# Revit family: 306_668fb259bbc246529dc69d010db632
name_source: partatom
category: Pipe Accessories
units: mm (PartAtom-declared; Revit-internal decimal feet)

## family parameters
Always vertical = Yes
Cut with Voids When Loaded = No
Part Type = Valve - Breaks Into
Round Connector Dimension = Use Diameter
Shared = No
Work Plane-Based = No

## types (57) — shared parameters
Description = 6-way characterised control valve, Internal thread
L2D_Min = 3048 mm  [stored 10 ft]
Manufacturer = Belimo
QmdConnectorList = 301;D;302;D;303;D;304;D;305;D;306;D
R3 = 10 mm  [stored 0.0328084 ft]
R5 = 15 mm  [stored 0.0492126 ft]
S1 = 43 mm  [stored 0.141076 ft]
S2 = 22 mm  [stored 0.0721785 ft]
S3 = 42 mm  [stored 0.137795 ft]
magiPartTypeId = 306
magiProductFamilyId = 668fb259bbc246529dc69d010db632

## per-type parameters (varying)
| type | CenSd_R_6 | D | H | H1 | H2 | H3 | H3__ve | L1 | L1__ve | L2 | L2D | L2__ve | LL | LY1 | LY1__ve | R | R1 | R2 | W2D | magiProductId |
| R3015-1-1-B2 | 10 mm  [stored 0.0328084 ft] | 15 mm | 119 mm  [stored 0.39042 ft] | 45 mm  [stored 0.147638 ft] | 47 mm  [stored 0.154199 ft] | 114 mm  [stored 0.374016 ft] | -114 mm  [stored -0.374016 ft] | 16 mm | -16 mm | 32 mm  [stored 0.104987 ft] | 79 mm | -32 mm | 40 mm  [stored 0.131234 ft] | 15 mm  [stored 0.0492126 ft] | -15 mm  [stored -0.0492126 ft] | 11 mm  [stored 0.0360892 ft] | 9 mm  [stored 0.0295276 ft] | 18 mm | 15 mm  [stored 0.0492126 ft] | 03fa744958c748f3845fa2f35dbf64 |
| R3020-P63-4-B2 | 13 mm | 20 mm | 148 mm  [stored 0.485564 ft] | 59 mm  [stored 0.19357 ft] | 54 mm  [stored 0.177165 ft] | 143 mm  [stored 0.46916 ft] | -143 mm  [stored -0.46916 ft] | 20 mm  [stored 0.0656168 ft] | -20 mm  [stored -0.0656168 ft] | 40 mm  [stored 0.131234 ft] | 100 mm  [stored 0.328084 ft] | -40 mm  [stored -0.131234 ft] | 50 mm  [stored 0.164042 ft] | 18 mm | -18 mm | 15 mm  [stored 0.0492126 ft] | 13 mm | 25 mm  [stored 0.082021 ft] | 20 mm  [stored 0.0656168 ft] | 66261c9dc02143649f8cac8046c0c7 |
| R3020-P63-2P5-B2 | 13 mm | 20 mm | 148 mm  [stored 0.485564 ft] | 59 mm  [stored 0.19357 ft] | 54 mm  [stored 0.177165 ft] | 143 mm  [stored 0.46916 ft] | -143 mm  [stored -0.46916 ft] | 20 mm  [stored 0.0656168 ft] | -20 mm  [stored -0.0656168 ft] | 40 mm  [stored 0.131234 ft] | 100 mm  [stored 0.328084 ft] | -40 mm  [stored -0.131234 ft] | 50 mm  [stored 0.164042 ft] | 18 mm | -18 mm | 15 mm  [stored 0.0492126 ft] | 13 mm | 25 mm  [stored 0.082021 ft] | 20 mm  [stored 0.0656168 ft] | 6e03b1389a624df6b33623b2063c5b |
| R3020-P63-1P6-B2 | 13 mm | 20 mm | 148 mm  [stored 0.485564 ft] | 59 mm  [stored 0.19357 ft] | 54 mm  [stored 0.177165 ft] | 143 mm  [stored 0.46916 ft] | -143 mm  [stored -0.46916 ft] | 20 mm  [stored 0.0656168 ft] | -20 mm  [stored -0.0656168 ft] | 40 mm  [stored 0.131234 ft] | 100 mm  [stored 0.328084 ft] | -40 mm  [stored -0.131234 ft] | 50 mm  [stored 0.164042 ft] | 18 mm | -18 mm | 15 mm  [stored 0.0492126 ft] | 13 mm | 25 mm  [stored 0.082021 ft] | 20 mm  [stored 0.0656168 ft] | fbef73f2dd7a4f4cae0204b01a27d9 |
| R3020-4-P63-B2 | 13 mm | 20 mm | 148 mm  [stored 0.485564 ft] | 59 mm  [stored 0.19357 ft] | 54 mm  [stored 0.177165 ft] | 143 mm  [stored 0.46916 ft] | -143 mm  [stored -0.46916 ft] | 20 mm  [stored 0.0656168 ft] | -20 mm  [stored -0.0656168 ft] | 40 mm  [stored 0.131234 ft] | 100 mm  [stored 0.328084 ft] | -40 mm  [stored -0.131234 ft] | 50 mm  [stored 0.164042 ft] | 18 mm | -18 mm | 15 mm  [stored 0.0492126 ft] | 13 mm | 25 mm  [stored 0.082021 ft] | 20 mm  [stored 0.0656168 ft] | ab1cd6763b854cb2a57e6034a10ecb |
| R3020-4-4-B2 | 13 mm | 20 mm | 148 mm  [stored 0.485564 ft] | 59 mm  [stored 0.19357 ft] | 54 mm  [stored 0.177165 ft] | 143 mm  [stored 0.46916 ft] | -143 mm  [stored -0.46916 ft] | 20 mm  [stored 0.0656168 ft] | -20 mm  [stored -0.0656168 ft] | 40 mm  [stored 0.131234 ft] | 100 mm  [stored 0.328084 ft] | -40 mm  [stored -0.131234 ft] | 50 mm  [stored 0.164042 ft] | 18 mm | -18 mm | 15 mm  [stored 0.0492126 ft] | 13 mm | 25 mm  [stored 0.082021 ft] | 20 mm  [stored 0.0656168 ft] | 5eca1c81c0fd4f1fafaa62e16ba6c2 |
| R3020-4-2P5-B2 | 13 mm | 20 mm | 148 mm  [stored 0.485564 ft] | 59 mm  [stored 0.19357 ft] | 54 mm  [stored 0.177165 ft] | 143 mm  [stored 0.46916 ft] | -143 mm  [stored -0.46916 ft] | 20 mm  [stored 0.0656168 ft] | -20 mm  [stored -0.0656168 ft] | 40 mm  [stored 0.131234 ft] | 100 mm  [stored 0.328084 ft] | -40 mm  [stored -0.131234 ft] | 50 mm  [stored 0.164042 ft] | 18 mm | -18 mm | 15 mm  [stored 0.0492126 ft] | 13 mm | 25 mm  [stored 0.082021 ft] | 20 mm  [stored 0.0656168 ft] | 8c2a2468e35046a99a0da62e88bc71 |
| R3020-4-1P6-B2 | 13 mm | 20 mm | 148 mm  [stored 0.485564 ft] | 59 mm  [stored 0.19357 ft] | 54 mm  [stored 0.177165 ft] | 143 mm  [stored 0.46916 ft] | -143 mm  [stored -0.46916 ft] | 20 mm  [stored 0.0656168 ft] | -20 mm  [stored -0.0656168 ft] | 40 mm  [stored 0.131234 ft] | 100 mm  [stored 0.328084 ft] | -40 mm  [stored -0.131234 ft] | 50 mm  [stored 0.164042 ft] | 18 mm | -18 mm | 15 mm  [stored 0.0492126 ft] | 13 mm | 25 mm  [stored 0.082021 ft] | 20 mm  [stored 0.0656168 ft] | 6e0713c00b33463ea5d84b7bfd9a89 |
| R3020-4-1-B2 | 13 mm | 20 mm | 148 mm  [stored 0.485564 ft] | 59 mm  [stored 0.19357 ft] | 54 mm  [stored 0.177165 ft] | 143 mm  [stored 0.46916 ft] | -143 mm  [stored -0.46916 ft] | 20 mm  [stored 0.0656168 ft] | -20 mm  [stored -0.0656168 ft] | 40 mm  [stored 0.131234 ft] | 100 mm  [stored 0.328084 ft] | -40 mm  [stored -0.131234 ft] | 50 mm  [stored 0.164042 ft] | 18 mm | -18 mm | 15 mm  [stored 0.0492126 ft] | 13 mm | 25 mm  [stored 0.082021 ft] | 20 mm  [stored 0.0656168 ft] | cf51fe3bf48d42a19b5262bd151528 |
| R3020-2P5-P63-B2 | 13 mm | 20 mm | 148 mm  [stored 0.485564 ft] | 59 mm  [stored 0.19357 ft] | 54 mm  [stored 0.177165 ft] | 143 mm  [stored 0.46916 ft] | -143 mm  [stored -0.46916 ft] | 20 mm  [stored 0.0656168 ft] | -20 mm  [stored -0.0656168 ft] | 40 mm  [stored 0.131234 ft] | 100 mm  [stored 0.328084 ft] | -40 mm  [stored -0.131234 ft] | 50 mm  [stored 0.164042 ft] | 18 mm | -18 mm | 15 mm  [stored 0.0492126 ft] | 13 mm | 25 mm  [stored 0.082021 ft] | 20 mm  [stored 0.0656168 ft] | 087235409c174f2a97f6a175d805da |
| R3020-2P5-4-B2 | 13 mm | 20 mm | 148 mm  [stored 0.485564 ft] | 59 mm  [stored 0.19357 ft] | 54 mm  [stored 0.177165 ft] | 143 mm  [stored 0.46916 ft] | -143 mm  [stored -0.46916 ft] | 20 mm  [stored 0.0656168 ft] | -20 mm  [stored -0.0656168 ft] | 40 mm  [stored 0.131234 ft] | 100 mm  [stored 0.328084 ft] | -40 mm  [stored -0.131234 ft] | 50 mm  [stored 0.164042 ft] | 18 mm | -18 mm | 15 mm  [stored 0.0492126 ft] | 13 mm | 25 mm  [stored 0.082021 ft] | 20 mm  [stored 0.0656168 ft] | 58d16455c4a143a0a09fdc7f0ee0a8 |
| R3020-2P5-2P5-B2 | 13 mm | 20 mm | 148 mm  [stored 0.485564 ft] | 59 mm  [stored 0.19357 ft] | 54 mm  [stored 0.177165 ft] | 143 mm  [stored 0.46916 ft] | -143 mm  [stored -0.46916 ft] | 20 mm  [stored 0.0656168 ft] | -20 mm  [stored -0.0656168 ft] | 40 mm  [stored 0.131234 ft] | 100 mm  [stored 0.328084 ft] | -40 mm  [stored -0.131234 ft] | 50 mm  [stored 0.164042 ft] | 18 mm | -18 mm | 15 mm  [stored 0.0492126 ft] | 13 mm | 25 mm  [stored 0.082021 ft] | 20 mm  [stored 0.0656168 ft] | 091caa0dfde748a884ceec14c542ad |
| R3020-2P5-1P6-B2 | 13 mm | 20 mm | 148 mm  [stored 0.485564 ft] | 59 mm  [stored 0.19357 ft] | 54 mm  [stored 0.177165 ft] | 143 mm  [stored 0.46916 ft] | -143 mm  [stored -0.46916 ft] | 20 mm  [stored 0.0656168 ft] | -20 mm  [stored -0.0656168 ft] | 40 mm  [stored 0.131234 ft] | 100 mm  [stored 0.328084 ft] | -40 mm  [stored -0.131234 ft] | 50 mm  [stored 0.164042 ft] | 18 mm | -18 mm | 15 mm  [stored 0.0492126 ft] | 13 mm | 25 mm  [stored 0.082021 ft] | 20 mm  [stored 0.0656168 ft] | 1ec0d4dad9a34521b66bef19604ba6 |
| R3020-2P5-1-B2 | 13 mm | 20 mm | 148 mm  [stored 0.485564 ft] | 59 mm  [stored 0.19357 ft] | 54 mm  [stored 0.177165 ft] | 143 mm  [stored 0.46916 ft] | -143 mm  [stored -0.46916 ft] | 20 mm  [stored 0.0656168 ft] | -20 mm  [stored -0.0656168 ft] | 40 mm  [stored 0.131234 ft] | 100 mm  [stored 0.328084 ft] | -40 mm  [stored -0.131234 ft] | 50 mm  [stored 0.164042 ft] | 18 mm | -18 mm | 15 mm  [stored 0.0492126 ft] | 13 mm | 25 mm  [stored 0.082021 ft] | 20 mm  [stored 0.0656168 ft] | cbbfb14f2a6e4f6f92310ec71a4552 |
| R3020-1P6-P63-B2 | 13 mm | 20 mm | 148 mm  [stored 0.485564 ft] | 59 mm  [stored 0.19357 ft] | 54 mm  [stored 0.177165 ft] | 143 mm  [stored 0.46916 ft] | -143 mm  [stored -0.46916 ft] | 20 mm  [stored 0.0656168 ft] | -20 mm  [stored -0.0656168 ft] | 40 mm  [stored 0.131234 ft] | 100 mm  [stored 0.328084 ft] | -40 mm  [stored -0.131234 ft] | 50 mm  [stored 0.164042 ft] | 18 mm | -18 mm | 15 mm  [stored 0.0492126 ft] | 13 mm | 25 mm  [stored 0.082021 ft] | 20 mm  [stored 0.0656168 ft] | 7b8e98678cfe4800af13abc20189e0 |
| R3020-1P6-4-B2 | 13 mm | 20 mm | 148 mm  [stored 0.485564 ft] | 59 mm  [stored 0.19357 ft] | 54 mm  [stored 0.177165 ft] | 143 mm  [stored 0.46916 ft] | -143 mm  [stored -0.46916 ft] | 20 mm  [stored 0.0656168 ft] | -20 mm  [stored -0.0656168 ft] | 40 mm  [stored 0.131234 ft] | 100 mm  [stored 0.328084 ft] | -40 mm  [stored -0.131234 ft] | 50 mm  [stored 0.164042 ft] | 18 mm | -18 mm | 15 mm  [stored 0.0492126 ft] | 13 mm | 25 mm  [stored 0.082021 ft] | 20 mm  [stored 0.0656168 ft] | 45ff41b9d2724979a5d0f47ae0925d |
| R3020-1P6-2P5-B2 | 13 mm | 20 mm | 148 mm  [stored 0.485564 ft] | 59 mm  [stored 0.19357 ft] | 54 mm  [stored 0.177165 ft] | 143 mm  [stored 0.46916 ft] | -143 mm  [stored -0.46916 ft] | 20 mm  [stored 0.0656168 ft] | -20 mm  [stored -0.0656168 ft] | 40 mm  [stored 0.131234 ft] | 100 mm  [stored 0.328084 ft] | -40 mm  [stored -0.131234 ft] | 50 mm  [stored 0.164042 ft] | 18 mm | -18 mm | 15 mm  [stored 0.0492126 ft] | 13 mm | 25 mm  [stored 0.082021 ft] | 20 mm  [stored 0.0656168 ft] | f1756c487f944601a2d215f7d87f2f |
| R3020-1P6-1P6-B2 | 13 mm | 20 mm | 148 mm  [stored 0.485564 ft] | 59 mm  [stored 0.19357 ft] | 54 mm  [stored 0.177165 ft] | 143 mm  [stored 0.46916 ft] | -143 mm  [stored -0.46916 ft] | 20 mm  [stored 0.0656168 ft] | -20 mm  [stored -0.0656168 ft] | 40 mm  [stored 0.131234 ft] | 100 mm  [stored 0.328084 ft] | -40 mm  [stored -0.131234 ft] | 50 mm  [stored 0.164042 ft] | 18 mm | -18 mm | 15 mm  [stored 0.0492126 ft] | 13 mm | 25 mm  [stored 0.082021 ft] | 20 mm  [stored 0.0656168 ft] | 7127969a5df24b65b1b6c93429b122 |
| R3020-1P6-1-B2 | 13 mm | 20 mm | 148 mm  [stored 0.485564 ft] | 59 mm  [stored 0.19357 ft] | 54 mm  [stored 0.177165 ft] | 143 mm  [stored 0.46916 ft] | -143 mm  [stored -0.46916 ft] | 20 mm  [stored 0.0656168 ft] | -20 mm  [stored -0.0656168 ft] | 40 mm  [stored 0.131234 ft] | 100 mm  [stored 0.328084 ft] | -40 mm  [stored -0.131234 ft] | 50 mm  [stored 0.164042 ft] | 18 mm | -18 mm | 15 mm  [stored 0.0492126 ft] | 13 mm | 25 mm  [stored 0.082021 ft] | 20 mm  [stored 0.0656168 ft] | 04216d9b90214d689f6043f1f76601 |
| R3020-1-4-B2 | 13 mm | 20 mm | 148 mm  [stored 0.485564 ft] | 59 mm  [stored 0.19357 ft] | 54 mm  [stored 0.177165 ft] | 143 mm  [stored 0.46916 ft] | -143 mm  [stored -0.46916 ft] | 20 mm  [stored 0.0656168 ft] | -20 mm  [stored -0.0656168 ft] | 40 mm  [stored 0.131234 ft] | 100 mm  [stored 0.328084 ft] | -40 mm  [stored -0.131234 ft] | 50 mm  [stored 0.164042 ft] | 18 mm | -18 mm | 15 mm  [stored 0.0492126 ft] | 13 mm | 25 mm  [stored 0.082021 ft] | 20 mm  [stored 0.0656168 ft] | 5b218b8cceb043d2b06aa8edcaf6e1 |
| R3020-1-2P5-B2 | 13 mm | 20 mm | 148 mm  [stored 0.485564 ft] | 59 mm  [stored 0.19357 ft] | 54 mm  [stored 0.177165 ft] | 143 mm  [stored 0.46916 ft] | -143 mm  [stored -0.46916 ft] | 20 mm  [stored 0.0656168 ft] | -20 mm  [stored -0.0656168 ft] | 40 mm  [stored 0.131234 ft] | 100 mm  [stored 0.328084 ft] | -40 mm  [stored -0.131234 ft] | 50 mm  [stored 0.164042 ft] | 18 mm | -18 mm | 15 mm  [stored 0.0492126 ft] | 13 mm | 25 mm  [stored 0.082021 ft] | 20 mm  [stored 0.0656168 ft] | bfc6b6497ea541fb84d5439e98900b |
| R3020-1-1P6-B2 | 13 mm | 20 mm | 148 mm  [stored 0.485564 ft] | 59 mm  [stored 0.19357 ft] | 54 mm  [stored 0.177165 ft] | 143 mm  [stored 0.46916 ft] | -143 mm  [stored -0.46916 ft] | 20 mm  [stored 0.0656168 ft] | -20 mm  [stored -0.0656168 ft] | 40 mm  [stored 0.131234 ft] | 100 mm  [stored 0.328084 ft] | -40 mm  [stored -0.131234 ft] | 50 mm  [stored 0.164042 ft] | 18 mm | -18 mm | 15 mm  [stored 0.0492126 ft] | 13 mm | 25 mm  [stored 0.082021 ft] | 20 mm  [stored 0.0656168 ft] | ce7173b337024baeb85b954c41b218 |
| R3015-P63-P63-B2 | 10 mm  [stored 0.0328084 ft] | 15 mm | 119 mm  [stored 0.39042 ft] | 45 mm  [stored 0.147638 ft] | 47 mm  [stored 0.154199 ft] | 114 mm  [stored 0.374016 ft] | -114 mm  [stored -0.374016 ft] | 16 mm | -16 mm | 32 mm  [stored 0.104987 ft] | 79 mm | -32 mm | 40 mm  [stored 0.131234 ft] | 15 mm  [stored 0.0492126 ft] | -15 mm  [stored -0.0492126 ft] | 11 mm  [stored 0.0360892 ft] | 9 mm  [stored 0.0295276 ft] | 18 mm | 15 mm  [stored 0.0492126 ft] | 7708a9e4e3e14db296ec0452a3ea06 |
| R3015-P63-P4-B2 | 10 mm  [stored 0.0328084 ft] | 15 mm | 119 mm  [stored 0.39042 ft] | 45 mm  [stored 0.147638 ft] | 47 mm  [stored 0.154199 ft] | 114 mm  [stored 0.374016 ft] | -114 mm  [stored -0.374016 ft] | 16 mm | -16 mm | 32 mm  [stored 0.104987 ft] | 79 mm | -32 mm | 40 mm  [stored 0.131234 ft] | 15 mm  [stored 0.0492126 ft] | -15 mm  [stored -0.0492126 ft] | 11 mm  [stored 0.0360892 ft] | 9 mm  [stored 0.0295276 ft] | 18 mm | 15 mm  [stored 0.0492126 ft] | 9ac8c1c8ba6c4946bd0a40c48ac7d7 |
| R3015-P63-P25-B2 | 10 mm  [stored 0.0328084 ft] | 15 mm | 119 mm  [stored 0.39042 ft] | 45 mm  [stored 0.147638 ft] | 47 mm  [stored 0.154199 ft] | 114 mm  [stored 0.374016 ft] | -114 mm  [stored -0.374016 ft] | 16 mm | -16 mm | 32 mm  [stored 0.104987 ft] | 79 mm | -32 mm | 40 mm  [stored 0.131234 ft] | 15 mm  [stored 0.0492126 ft] | -15 mm  [stored -0.0492126 ft] | 11 mm  [stored 0.0360892 ft] | 9 mm  [stored 0.0295276 ft] | 18 mm | 15 mm  [stored 0.0492126 ft] | db04380f07ed40d99dcd1a924616eb |
| R3015-P63-1P8-B2 | 10 mm  [stored 0.0328084 ft] | 15 mm | 119 mm  [stored 0.39042 ft] | 45 mm  [stored 0.147638 ft] | 47 mm  [stored 0.154199 ft] | 114 mm  [stored 0.374016 ft] | -114 mm  [stored -0.374016 ft] | 16 mm | -16 mm | 32 mm  [stored 0.104987 ft] | 79 mm | -32 mm | 40 mm  [stored 0.131234 ft] | 15 mm  [stored 0.0492126 ft] | -15 mm  [stored -0.0492126 ft] | 11 mm  [stored 0.0360892 ft] | 9 mm  [stored 0.0295276 ft] | 18 mm | 15 mm  [stored 0.0492126 ft] | 716974af9d7e4c71980a3ceb5bcacc |
| R3015-P63-1P3-B2 | 10 mm  [stored 0.0328084 ft] | 15 mm | 119 mm  [stored 0.39042 ft] | 45 mm  [stored 0.147638 ft] | 47 mm  [stored 0.154199 ft] | 114 mm  [stored 0.374016 ft] | -114 mm  [stored -0.374016 ft] | 16 mm | -16 mm | 32 mm  [stored 0.104987 ft] | 79 mm | -32 mm | 40 mm  [stored 0.131234 ft] | 15 mm  [stored 0.0492126 ft] | -15 mm  [stored -0.0492126 ft] | 11 mm  [stored 0.0360892 ft] | 9 mm  [stored 0.0295276 ft] | 18 mm | 15 mm  [stored 0.0492126 ft] | 53b4a3d678a449c4982707f79ae4e7 |
| R3015-P63-1-B2 | 10 mm  [stored 0.0328084 ft] | 15 mm | 119 mm  [stored 0.39042 ft] | 45 mm  [stored 0.147638 ft] | 47 mm  [stored 0.154199 ft] | 114 mm  [stored 0.374016 ft] | -114 mm  [stored -0.374016 ft] | 16 mm | -16 mm | 32 mm  [stored 0.104987 ft] | 79 mm | -32 mm | 40 mm  [stored 0.131234 ft] | 15 mm  [stored 0.0492126 ft] | -15 mm  [stored -0.0492126 ft] | 11 mm  [stored 0.0360892 ft] | 9 mm  [stored 0.0295276 ft] | 18 mm | 15 mm  [stored 0.0492126 ft] | da1d95099e2c4361ae2f9d947ad547 |
| R3015-P4-P63-B2 | 10 mm  [stored 0.0328084 ft] | 15 mm | 119 mm  [stored 0.39042 ft] | 45 mm  [stored 0.147638 ft] | 47 mm  [stored 0.154199 ft] | 114 mm  [stored 0.374016 ft] | -114 mm  [stored -0.374016 ft] | 16 mm | -16 mm | 32 mm  [stored 0.104987 ft] | 79 mm | -32 mm | 40 mm  [stored 0.131234 ft] | 15 mm  [stored 0.0492126 ft] | -15 mm  [stored -0.0492126 ft] | 11 mm  [stored 0.0360892 ft] | 9 mm  [stored 0.0295276 ft] | 18 mm | 15 mm  [stored 0.0492126 ft] | 51f427faca8a42b3ba5ebe70674f41 |
| R3015-P4-P4-B2 | 10 mm  [stored 0.0328084 ft] | 15 mm | 119 mm  [stored 0.39042 ft] | 45 mm  [stored 0.147638 ft] | 47 mm  [stored 0.154199 ft] | 114 mm  [stored 0.374016 ft] | -114 mm  [stored -0.374016 ft] | 16 mm | -16 mm | 32 mm  [stored 0.104987 ft] | 79 mm | -32 mm | 40 mm  [stored 0.131234 ft] | 15 mm  [stored 0.0492126 ft] | -15 mm  [stored -0.0492126 ft] | 11 mm  [stored 0.0360892 ft] | 9 mm  [stored 0.0295276 ft] | 18 mm | 15 mm  [stored 0.0492126 ft] | d58cdffd2ecc43889e93d59264498d |
| R3015-P4-P25-B2 | 10 mm  [stored 0.0328084 ft] | 15 mm | 119 mm  [stored 0.39042 ft] | 45 mm  [stored 0.147638 ft] | 47 mm  [stored 0.154199 ft] | 114 mm  [stored 0.374016 ft] | -114 mm  [stored -0.374016 ft] | 16 mm | -16 mm | 32 mm  [stored 0.104987 ft] | 79 mm | -32 mm | 40 mm  [stored 0.131234 ft] | 15 mm  [stored 0.0492126 ft] | -15 mm  [stored -0.0492126 ft] | 11 mm  [stored 0.0360892 ft] | 9 mm  [stored 0.0295276 ft] | 18 mm | 15 mm  [stored 0.0492126 ft] | a59cf75667fb487e826b3ffab89c25 |
| R3015-P4-1P8-B2 | 10 mm  [stored 0.0328084 ft] | 15 mm | 119 mm  [stored 0.39042 ft] | 45 mm  [stored 0.147638 ft] | 47 mm  [stored 0.154199 ft] | 114 mm  [stored 0.374016 ft] | -114 mm  [stored -0.374016 ft] | 16 mm | -16 mm | 32 mm  [stored 0.104987 ft] | 79 mm | -32 mm | 40 mm  [stored 0.131234 ft] | 15 mm  [stored 0.0492126 ft] | -15 mm  [stored -0.0492126 ft] | 11 mm  [stored 0.0360892 ft] | 9 mm  [stored 0.0295276 ft] | 18 mm | 15 mm  [stored 0.0492126 ft] | 838d19e88f7b48b4896f9642db5711 |
| R3015-P4-1P3-B2 | 10 mm  [stored 0.0328084 ft] | 15 mm | 119 mm  [stored 0.39042 ft] | 45 mm  [stored 0.147638 ft] | 47 mm  [stored 0.154199 ft] | 114 mm  [stored 0.374016 ft] | -114 mm  [stored -0.374016 ft] | 16 mm | -16 mm | 32 mm  [stored 0.104987 ft] | 79 mm | -32 mm | 40 mm  [stored 0.131234 ft] | 15 mm  [stored 0.0492126 ft] | -15 mm  [stored -0.0492126 ft] | 11 mm  [stored 0.0360892 ft] | 9 mm  [stored 0.0295276 ft] | 18 mm | 15 mm  [stored 0.0492126 ft] | 332b415680ba4d87aebb7987f36cee |
| R3015-P4-1-B2 | 10 mm  [stored 0.0328084 ft] | 15 mm | 119 mm  [stored 0.39042 ft] | 45 mm  [stored 0.147638 ft] | 47 mm  [stored 0.154199 ft] | 114 mm  [stored 0.374016 ft] | -114 mm  [stored -0.374016 ft] | 16 mm | -16 mm | 32 mm  [stored 0.104987 ft] | 79 mm | -32 mm | 40 mm  [stored 0.131234 ft] | 15 mm  [stored 0.0492126 ft] | -15 mm  [stored -0.0492126 ft] | 11 mm  [stored 0.0360892 ft] | 9 mm  [stored 0.0295276 ft] | 18 mm | 15 mm  [stored 0.0492126 ft] | e9ddc90427134804bca86574a02143 |
| R3015-P25-P63-B2 | 10 mm  [stored 0.0328084 ft] | 15 mm | 119 mm  [stored 0.39042 ft] | 45 mm  [stored 0.147638 ft] | 47 mm  [stored 0.154199 ft] | 114 mm  [stored 0.374016 ft] | -114 mm  [stored -0.374016 ft] | 16 mm | -16 mm | 32 mm  [stored 0.104987 ft] | 79 mm | -32 mm | 40 mm  [stored 0.131234 ft] | 15 mm  [stored 0.0492126 ft] | -15 mm  [stored -0.0492126 ft] | 11 mm  [stored 0.0360892 ft] | 9 mm  [stored 0.0295276 ft] | 18 mm | 15 mm  [stored 0.0492126 ft] | 2ada7fccbf6c45f18df2853344e53d |
| R3015-P25-P4-B2 | 10 mm  [stored 0.0328084 ft] | 15 mm | 119 mm  [stored 0.39042 ft] | 45 mm  [stored 0.147638 ft] | 47 mm  [stored 0.154199 ft] | 114 mm  [stored 0.374016 ft] | -114 mm  [stored -0.374016 ft] | 16 mm | -16 mm | 32 mm  [stored 0.104987 ft] | 79 mm | -32 mm | 40 mm  [stored 0.131234 ft] | 15 mm  [stored 0.0492126 ft] | -15 mm  [stored -0.0492126 ft] | 11 mm  [stored 0.0360892 ft] | 9 mm  [stored 0.0295276 ft] | 18 mm | 15 mm  [stored 0.0492126 ft] | de6999a60d0941b5bbad0c57cd129d |
| R3015-P25-P25-B2 | 10 mm  [stored 0.0328084 ft] | 15 mm | 119 mm  [stored 0.39042 ft] | 45 mm  [stored 0.147638 ft] | 47 mm  [stored 0.154199 ft] | 114 mm  [stored 0.374016 ft] | -114 mm  [stored -0.374016 ft] | 16 mm | -16 mm | 32 mm  [stored 0.104987 ft] | 79 mm | -32 mm | 40 mm  [stored 0.131234 ft] | 15 mm  [stored 0.0492126 ft] | -15 mm  [stored -0.0492126 ft] | 11 mm  [stored 0.0360892 ft] | 9 mm  [stored 0.0295276 ft] | 18 mm | 15 mm  [stored 0.0492126 ft] | 524d8532bb9e401d80915f57478390 |
| R3015-P25-1P8-B2 | 10 mm  [stored 0.0328084 ft] | 15 mm | 119 mm  [stored 0.39042 ft] | 45 mm  [stored 0.147638 ft] | 47 mm  [stored 0.154199 ft] | 114 mm  [stored 0.374016 ft] | -114 mm  [stored -0.374016 ft] | 16 mm | -16 mm | 32 mm  [stored 0.104987 ft] | 79 mm | -32 mm | 40 mm  [stored 0.131234 ft] | 15 mm  [stored 0.0492126 ft] | -15 mm  [stored -0.0492126 ft] | 11 mm  [stored 0.0360892 ft] | 9 mm  [stored 0.0295276 ft] | 18 mm | 15 mm  [stored 0.0492126 ft] | 6f247674cfa14effa4aa32a7d19eac |
| R3015-P25-1P3-B2 | 10 mm  [stored 0.0328084 ft] | 15 mm | 119 mm  [stored 0.39042 ft] | 45 mm  [stored 0.147638 ft] | 47 mm  [stored 0.154199 ft] | 114 mm  [stored 0.374016 ft] | -114 mm  [stored -0.374016 ft] | 16 mm | -16 mm | 32 mm  [stored 0.104987 ft] | 79 mm | -32 mm | 40 mm  [stored 0.131234 ft] | 15 mm  [stored 0.0492126 ft] | -15 mm  [stored -0.0492126 ft] | 11 mm  [stored 0.0360892 ft] | 9 mm  [stored 0.0295276 ft] | 18 mm | 15 mm  [stored 0.0492126 ft] | 680b0ce2c18740a9a0250d86df942c |
| R3015-P25-1-B2 | 10 mm  [stored 0.0328084 ft] | 15 mm | 119 mm  [stored 0.39042 ft] | 45 mm  [stored 0.147638 ft] | 47 mm  [stored 0.154199 ft] | 114 mm  [stored 0.374016 ft] | -114 mm  [stored -0.374016 ft] | 16 mm | -16 mm | 32 mm  [stored 0.104987 ft] | 79 mm | -32 mm | 40 mm  [stored 0.131234 ft] | 15 mm  [stored 0.0492126 ft] | -15 mm  [stored -0.0492126 ft] | 11 mm  [stored 0.0360892 ft] | 9 mm  [stored 0.0295276 ft] | 18 mm | 15 mm  [stored 0.0492126 ft] | b06ac9aa10974affa13b7a86db2574 |
| R3015-1P8-P63-B2 | 10 mm  [stored 0.0328084 ft] | 15 mm | 119 mm  [stored 0.39042 ft] | 45 mm  [stored 0.147638 ft] | 47 mm  [stored 0.154199 ft] | 114 mm  [stored 0.374016 ft] | -114 mm  [stored -0.374016 ft] | 16 mm | -16 mm | 32 mm  [stored 0.104987 ft] | 79 mm | -32 mm | 40 mm  [stored 0.131234 ft] | 15 mm  [stored 0.0492126 ft] | -15 mm  [stored -0.0492126 ft] | 11 mm  [stored 0.0360892 ft] | 9 mm  [stored 0.0295276 ft] | 18 mm | 15 mm  [stored 0.0492126 ft] | f3a2c67d0dc54f3589b27fbcb569bd |
| R3015-1P8-P4-B2 | 10 mm  [stored 0.0328084 ft] | 15 mm | 119 mm  [stored 0.39042 ft] | 45 mm  [stored 0.147638 ft] | 47 mm  [stored 0.154199 ft] | 114 mm  [stored 0.374016 ft] | -114 mm  [stored -0.374016 ft] | 16 mm | -16 mm | 32 mm  [stored 0.104987 ft] | 79 mm | -32 mm | 40 mm  [stored 0.131234 ft] | 15 mm  [stored 0.0492126 ft] | -15 mm  [stored -0.0492126 ft] | 11 mm  [stored 0.0360892 ft] | 9 mm  [stored 0.0295276 ft] | 18 mm | 15 mm  [stored 0.0492126 ft] | 03faa52287d7461291c86972750d05 |
| R3015-1P8-P25-B2 | 10 mm  [stored 0.0328084 ft] | 15 mm | 119 mm  [stored 0.39042 ft] | 45 mm  [stored 0.147638 ft] | 47 mm  [stored 0.154199 ft] | 114 mm  [stored 0.374016 ft] | -114 mm  [stored -0.374016 ft] | 16 mm | -16 mm | 32 mm  [stored 0.104987 ft] | 79 mm | -32 mm | 40 mm  [stored 0.131234 ft] | 15 mm  [stored 0.0492126 ft] | -15 mm  [stored -0.0492126 ft] | 11 mm  [stored 0.0360892 ft] | 9 mm  [stored 0.0295276 ft] | 18 mm | 15 mm  [stored 0.0492126 ft] | 1a3ba31a7ef74fe09ed31aea571015 |
| R3015-1P8-1P8-B2 | 10 mm  [stored 0.0328084 ft] | 15 mm | 119 mm  [stored 0.39042 ft] | 45 mm  [stored 0.147638 ft] | 47 mm  [stored 0.154199 ft] | 114 mm  [stored 0.374016 ft] | -114 mm  [stored -0.374016 ft] | 16 mm | -16 mm | 32 mm  [stored 0.104987 ft] | 79 mm | -32 mm | 40 mm  [stored 0.131234 ft] | 15 mm  [stored 0.0492126 ft] | -15 mm  [stored -0.0492126 ft] | 11 mm  [stored 0.0360892 ft] | 9 mm  [stored 0.0295276 ft] | 18 mm | 15 mm  [stored 0.0492126 ft] | 3647ae1cdb7c433b953047a92a15e2 |
| R3015-1P8-1P3-B2 | 10 mm  [stored 0.0328084 ft] | 15 mm | 119 mm  [stored 0.39042 ft] | 45 mm  [stored 0.147638 ft] | 47 mm  [stored 0.154199 ft] | 114 mm  [stored 0.374016 ft] | -114 mm  [stored -0.374016 ft] | 16 mm | -16 mm | 32 mm  [stored 0.104987 ft] | 79 mm | -32 mm | 40 mm  [stored 0.131234 ft] | 15 mm  [stored 0.0492126 ft] | -15 mm  [stored -0.0492126 ft] | 11 mm  [stored 0.0360892 ft] | 9 mm  [stored 0.0295276 ft] | 18 mm | 15 mm  [stored 0.0492126 ft] | 2c9227ab23f44f5aa0f782351bc2e3 |
| R3015-1P8-1-B2 | 10 mm  [stored 0.0328084 ft] | 15 mm | 119 mm  [stored 0.39042 ft] | 45 mm  [stored 0.147638 ft] | 47 mm  [stored 0.154199 ft] | 114 mm  [stored 0.374016 ft] | -114 mm  [stored -0.374016 ft] | 16 mm | -16 mm | 32 mm  [stored 0.104987 ft] | 79 mm | -32 mm | 40 mm  [stored 0.131234 ft] | 15 mm  [stored 0.0492126 ft] | -15 mm  [stored -0.0492126 ft] | 11 mm  [stored 0.0360892 ft] | 9 mm  [stored 0.0295276 ft] | 18 mm | 15 mm  [stored 0.0492126 ft] | faeafafb70fc467ba931b8f53bce3e |
| R3015-1-P63-B2 | 10 mm  [stored 0.0328084 ft] | 15 mm | 119 mm  [stored 0.39042 ft] | 45 mm  [stored 0.147638 ft] | 47 mm  [stored 0.154199 ft] | 114 mm  [stored 0.374016 ft] | -114 mm  [stored -0.374016 ft] | 16 mm | -16 mm | 32 mm  [stored 0.104987 ft] | 79 mm | -32 mm | 40 mm  [stored 0.131234 ft] | 15 mm  [stored 0.0492126 ft] | -15 mm  [stored -0.0492126 ft] | 11 mm  [stored 0.0360892 ft] | 9 mm  [stored 0.0295276 ft] | 18 mm | 15 mm  [stored 0.0492126 ft] | 4f69d3babf6f4d14937ee6c66b482b |
| R3015-1-P4-B2 | 10 mm  [stored 0.0328084 ft] | 15 mm | 119 mm  [stored 0.39042 ft] | 45 mm  [stored 0.147638 ft] | 47 mm  [stored 0.154199 ft] | 114 mm  [stored 0.374016 ft] | -114 mm  [stored -0.374016 ft] | 16 mm | -16 mm | 32 mm  [stored 0.104987 ft] | 79 mm | -32 mm | 40 mm  [stored 0.131234 ft] | 15 mm  [stored 0.0492126 ft] | -15 mm  [stored -0.0492126 ft] | 11 mm  [stored 0.0360892 ft] | 9 mm  [stored 0.0295276 ft] | 18 mm | 15 mm  [stored 0.0492126 ft] | 15e3a13905cf4ce1a3b1e0cb60cbd7 |
| R3015-1P3-P63-B2 | 10 mm  [stored 0.0328084 ft] | 15 mm | 119 mm  [stored 0.39042 ft] | 45 mm  [stored 0.147638 ft] | 47 mm  [stored 0.154199 ft] | 114 mm  [stored 0.374016 ft] | -114 mm  [stored -0.374016 ft] | 16 mm | -16 mm | 32 mm  [stored 0.104987 ft] | 79 mm | -32 mm | 40 mm  [stored 0.131234 ft] | 15 mm  [stored 0.0492126 ft] | -15 mm  [stored -0.0492126 ft] | 11 mm  [stored 0.0360892 ft] | 9 mm  [stored 0.0295276 ft] | 18 mm | 15 mm  [stored 0.0492126 ft] | a357b877825b444cbd7e0201632028 |
| R3015-1P3-P4-B2 | 10 mm  [stored 0.0328084 ft] | 15 mm | 119 mm  [stored 0.39042 ft] | 45 mm  [stored 0.147638 ft] | 47 mm  [stored 0.154199 ft] | 114 mm  [stored 0.374016 ft] | -114 mm  [stored -0.374016 ft] | 16 mm | -16 mm | 32 mm  [stored 0.104987 ft] | 79 mm | -32 mm | 40 mm  [stored 0.131234 ft] | 15 mm  [stored 0.0492126 ft] | -15 mm  [stored -0.0492126 ft] | 11 mm  [stored 0.0360892 ft] | 9 mm  [stored 0.0295276 ft] | 18 mm | 15 mm  [stored 0.0492126 ft] | 93530a5b29704ecba29b6fe1334aa8 |
| R3015-1P3-P25-B2 | 10 mm  [stored 0.0328084 ft] | 15 mm | 119 mm  [stored 0.39042 ft] | 45 mm  [stored 0.147638 ft] | 47 mm  [stored 0.154199 ft] | 114 mm  [stored 0.374016 ft] | -114 mm  [stored -0.374016 ft] | 16 mm | -16 mm | 32 mm  [stored 0.104987 ft] | 79 mm | -32 mm | 40 mm  [stored 0.131234 ft] | 15 mm  [stored 0.0492126 ft] | -15 mm  [stored -0.0492126 ft] | 11 mm  [stored 0.0360892 ft] | 9 mm  [stored 0.0295276 ft] | 18 mm | 15 mm  [stored 0.0492126 ft] | a7799576a9cb4fdd980911d6260af3 |
| R3015-1P3-1P8-B2 | 10 mm  [stored 0.0328084 ft] | 15 mm | 119 mm  [stored 0.39042 ft] | 45 mm  [stored 0.147638 ft] | 47 mm  [stored 0.154199 ft] | 114 mm  [stored 0.374016 ft] | -114 mm  [stored -0.374016 ft] | 16 mm | -16 mm | 32 mm  [stored 0.104987 ft] | 79 mm | -32 mm | 40 mm  [stored 0.131234 ft] | 15 mm  [stored 0.0492126 ft] | -15 mm  [stored -0.0492126 ft] | 11 mm  [stored 0.0360892 ft] | 9 mm  [stored 0.0295276 ft] | 18 mm | 15 mm  [stored 0.0492126 ft] | acaa2c7053c14af19caa541d7c62c7 |
| R3015-1P3-1P3-B2 | 10 mm  [stored 0.0328084 ft] | 15 mm | 119 mm  [stored 0.39042 ft] | 45 mm  [stored 0.147638 ft] | 47 mm  [stored 0.154199 ft] | 114 mm  [stored 0.374016 ft] | -114 mm  [stored -0.374016 ft] | 16 mm | -16 mm | 32 mm  [stored 0.104987 ft] | 79 mm | -32 mm | 40 mm  [stored 0.131234 ft] | 15 mm  [stored 0.0492126 ft] | -15 mm  [stored -0.0492126 ft] | 11 mm  [stored 0.0360892 ft] | 9 mm  [stored 0.0295276 ft] | 18 mm | 15 mm  [stored 0.0492126 ft] | e2541895408c4f089659d789862806 |
| R3015-1P3-1-B2 | 10 mm  [stored 0.0328084 ft] | 15 mm | 119 mm  [stored 0.39042 ft] | 45 mm  [stored 0.147638 ft] | 47 mm  [stored 0.154199 ft] | 114 mm  [stored 0.374016 ft] | -114 mm  [stored -0.374016 ft] | 16 mm | -16 mm | 32 mm  [stored 0.104987 ft] | 79 mm | -32 mm | 40 mm  [stored 0.131234 ft] | 15 mm  [stored 0.0492126 ft] | -15 mm  [stored -0.0492126 ft] | 11 mm  [stored 0.0360892 ft] | 9 mm  [stored 0.0295276 ft] | 18 mm | 15 mm  [stored 0.0492126 ft] | 3c63eba4c40846f4819acd903af803 |
| R3015-1-P25-B2 | 10 mm  [stored 0.0328084 ft] | 15 mm | 119 mm  [stored 0.39042 ft] | 45 mm  [stored 0.147638 ft] | 47 mm  [stored 0.154199 ft] | 114 mm  [stored 0.374016 ft] | -114 mm  [stored -0.374016 ft] | 16 mm | -16 mm | 32 mm  [stored 0.104987 ft] | 79 mm | -32 mm | 40 mm  [stored 0.131234 ft] | 15 mm  [stored 0.0492126 ft] | -15 mm  [stored -0.0492126 ft] | 11 mm  [stored 0.0360892 ft] | 9 mm  [stored 0.0295276 ft] | 18 mm | 15 mm  [stored 0.0492126 ft] | dcd6d3dfa66e47349c68b2fefb9de2 |
| R3015-1-1P8-B2 | 10 mm  [stored 0.0328084 ft] | 15 mm | 119 mm  [stored 0.39042 ft] | 45 mm  [stored 0.147638 ft] | 47 mm  [stored 0.154199 ft] | 114 mm  [stored 0.374016 ft] | -114 mm  [stored -0.374016 ft] | 16 mm | -16 mm | 32 mm  [stored 0.104987 ft] | 79 mm | -32 mm | 40 mm  [stored 0.131234 ft] | 15 mm  [stored 0.0492126 ft] | -15 mm  [stored -0.0492126 ft] | 11 mm  [stored 0.0360892 ft] | 9 mm  [stored 0.0295276 ft] | 18 mm | 15 mm  [stored 0.0492126 ft] | 6791030133c6487ab6b66f99dd0a0a |
| R3015-1-1P3-B2 | 10 mm  [stored 0.0328084 ft] | 15 mm | 119 mm  [stored 0.39042 ft] | 45 mm  [stored 0.147638 ft] | 47 mm  [stored 0.154199 ft] | 114 mm  [stored 0.374016 ft] | -114 mm  [stored -0.374016 ft] | 16 mm | -16 mm | 32 mm  [stored 0.104987 ft] | 79 mm | -32 mm | 40 mm  [stored 0.131234 ft] | 15 mm  [stored 0.0492126 ft] | -15 mm  [stored -0.0492126 ft] | 11 mm  [stored 0.0360892 ft] | 9 mm  [stored 0.0295276 ft] | 18 mm | 15 mm  [stored 0.0492126 ft] | 04aa048243ee4d4e9aa13f5ddbb3fe |

note: column(s) folded — value = type name in every type: MC Product Code

note: [stored X ft] marks values corroborated as IEEE doubles in the binary element streams (Revit-internal decimal feet)

## geometry (parser evidence)
native form markers: Blend x2, Sweep x3
no freeform markers — native parametric forms only
